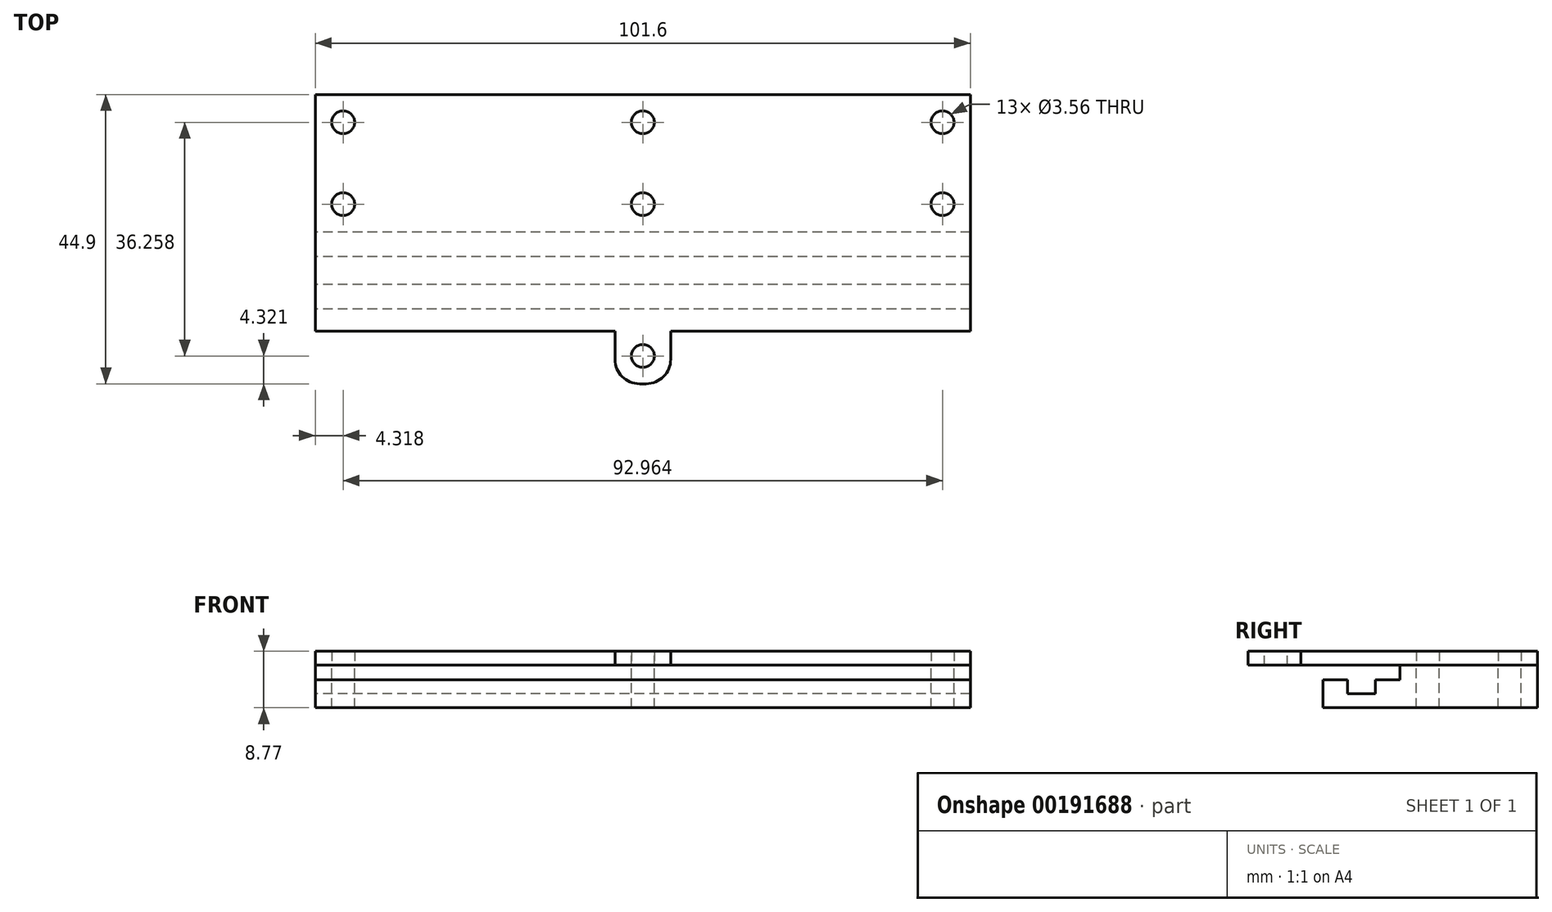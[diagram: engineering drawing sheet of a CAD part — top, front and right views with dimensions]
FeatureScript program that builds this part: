
annotation { "Feature Type Name" : "Feature", "Feature Type Description" : "" }
export const myFeature = defineFeature(function(context is Context, id is Id, definition is map)
    precondition{}
    {
        {
            var Q0;
            Q0=qCreatedBy(makeId("Right.planeOp"),FACE);
            var sketch = newSketch(context, id + "F0", { "sketchPlane" : qUnion([Q0])});
            skLineSegment(sketch, "E0.top", {"start": v(-6.45, -4.32) * mm, "end": v(26.83, -4.32) * mm});
            skLineSegment(sketch, "E0.left", {"start": v(-6.45, 0) * mm, "end": v(-6.45, -4.32) * mm});
            skLineSegment(sketch, "E0.right", {"start": v(26.83, 0) * mm, "end": v(26.83, -4.32) * mm});
            skLineSegment(sketch, "E1", {"start": v(-2.64, 0) * mm, "end": v(-2.64, -2.16) * mm});
            skLineSegment(sketch, "E2", {"start": v(-2.64, -2.16) * mm, "end": v(1.68, -2.16) * mm});
            skLineSegment(sketch, "E3", {"start": v(1.68, -2.16) * mm, "end": v(1.68, 0) * mm});
            skLineSegment(sketch, "E4", {"start": v(-6.45, 0) * mm, "end": v(-2.64, 0) * mm});
            skLineSegment(sketch, "E5", {"start": v(1.68, 0) * mm, "end": v(5.5, 0) * mm});
            skLineSegment(sketch, "E6", {"start": v(26.83, 0) * mm, "end": v(26.83, 2.29) * mm});
            skLineSegment(sketch, "E7", {"start": v(26.83, 2.29) * mm, "end": v(5.5, 2.29) * mm});
            skLineSegment(sketch, "E8", {"start": v(5.5, 2.29) * mm, "end": v(5.5, 0) * mm});
            skSolve(sketch);
        }
        {
            var Q0;
            Q0=makeQuery(id+"F0.imprint","IMPRINT",FACE,{"disambiguationData":[TD([[makeQuery(id+"F0.imprint","IMPRINT",EDGE,{"derivedFrom":sQuery(id+"F0.wireOp",EDGE,"E0.top")}),1.0]])]});
            extrude(context, id + "F1", {"entities" : qUnion([Q0]), "depth" : 101.6 * mm});
        }
        {
            var Q0;
            Q0=makeQuery(id+"F1.opExtrude","SWEPT_FACE",FACE,{"disambiguationData":[OSD([sQuery(id+"F0.wireOp",EDGE,"E7")])]});
            var sketch = newSketch(context, id + "F2", { "sketchPlane" : qUnion([Q0])});
            skCircle(sketch, "E9", {"center": v(97.28, 9.8) * mm, "radius": 1.78 * mm});
            skCircle(sketch, "E10", {"center": v(97.28, 22.5) * mm, "radius": 1.78 * mm});
            skCircle(sketch, "E11", {"center": v(4.32, 9.8) * mm, "radius": 1.78 * mm});
            skCircle(sketch, "E12", {"center": v(4.32, 22.5) * mm, "radius": 1.78 * mm});
            skCircle(sketch, "E13", {"center": v(50.8, 9.8) * mm, "radius": 1.78 * mm});
            skPoint(sketch, "E13.centerSnap0", {"position": v(50.8, 5.5) * mm});
            skCircle(sketch, "E14", {"center": v(50.8, 22.5) * mm, "radius": 1.78 * mm});
            skSolve(sketch);
        }
        {
            var Q0;
            Q0=qSketchRegion(id+"F2",true);
            extrude(context, id + "F3", {"entities" : qUnion([Q0]), "operationType" : NewBodyOperationType.REMOVE, "endBound" : BoundingType.THROUGH_ALL, "oppositeDirection" : true, "depth" : 25.4 * mm});
        }
        {
            var Q0;
            Q0=qCreatedBy(makeId("Right.planeOp"),FACE);
            var sketch = newSketch(context, id + "F4", { "sketchPlane" : qUnion([Q0])});
            skLineSegment(sketch, "E15", {"start": v(-9.88, 2.29) * mm, "end": v(-9.88, 4.45) * mm});
            skLineSegment(sketch, "E16.0", {"start": v(26.83, 2.29) * mm, "end": v(5.5, 2.29) * mm});
            skLineSegment(sketch, "E17", {"start": v(-9.88, 2.29) * mm, "end": v(26.83, 2.29) * mm});
            skLineSegment(sketch, "E18", {"start": v(26.83, 4.45) * mm, "end": v(26.83, 2.29) * mm});
            skLineSegment(sketch, "E19", {"start": v(26.83, 4.45) * mm, "end": v(-9.88, 4.45) * mm});
            skSolve(sketch);
        }
        {
            var Q0;
            {var subQ0=sQuery(id+"F4.wireOp",EDGE,"E15");Q0=makeQuery(id+"F4.imprint","IMPRINT",FACE,{"disambiguationData":[TD([[makeQuery(id+"F4.imprint","IMPRINT",EDGE,{"derivedFrom":subQ0}),-1.0]])]});}
            var Q1;
            Q1=makeQuery(id+"F1.opExtrude","CAP_FACE",FACE,{"disambiguationData":[OSD([sQuery(id+"F0.wireOp",EDGE,"E0.top"),sQuery(id+"F0.wireOp",EDGE,"E0.left"),sQuery(id+"F0.wireOp",EDGE,"E0.right"),sQuery(id+"F0.wireOp",EDGE,"E1"),sQuery(id+"F0.wireOp",EDGE,"E2"),sQuery(id+"F0.wireOp",EDGE,"E3"),sQuery(id+"F0.wireOp",EDGE,"E4"),sQuery(id+"F0.wireOp",EDGE,"E5"),sQuery(id+"F0.wireOp",EDGE,"E6"),sQuery(id+"F0.wireOp",EDGE,"E7"),sQuery(id+"F0.wireOp",EDGE,"E8")])],"isStart":false});
            extrude(context, id + "F5", {"entities" : qUnion([Q0]), "endBound" : BoundingType.UP_TO_SURFACE, "endBoundEntityFace" : qUnion([Q1]), "depth" : 25.4 * mm});
        }
        {
            var Q0;
            Q0=makeQuery(id+"F5.opExtrude","SWEPT_FACE",FACE,{"disambiguationData":[OSD([sQuery(id+"F4.wireOp",EDGE,"E17")])]});
            var sketch = newSketch(context, id + "F6", { "sketchPlane" : qUnion([Q0])});
            skCircle(sketch, "E20.0", {"center": v(97.28, -9.8) * mm, "radius": 1.78 * mm});
            skCircle(sketch, "E20.1", {"center": v(50.8, -9.8) * mm, "radius": 1.78 * mm});
            skCircle(sketch, "E20.2", {"center": v(4.32, -9.8) * mm, "radius": 1.78 * mm});
            skCircle(sketch, "E20.3", {"center": v(4.32, -22.5) * mm, "radius": 1.78 * mm});
            skCircle(sketch, "E20.4", {"center": v(50.8, -22.5) * mm, "radius": 1.78 * mm});
            skCircle(sketch, "E20.5", {"center": v(97.28, -22.5) * mm, "radius": 1.78 * mm});
            skSolve(sketch);
        }
        {
            var Q0;
            Q0=qSketchRegion(id+"F6",true);
            extrude(context, id + "F7", {"entities" : qUnion([Q0]), "operationType" : NewBodyOperationType.REMOVE, "endBound" : BoundingType.THROUGH_ALL, "oppositeDirection" : true, "depth" : 25.4 * mm});
        }
        {
            var Q0;
            Q0=makeQuery(id+"F5.opExtrude","SWEPT_FACE",FACE,{"disambiguationData":[OSD([sQuery(id+"F4.wireOp",EDGE,"E19")])]});
            var sketch = newSketch(context, id + "F8", { "sketchPlane" : qUnion([Q0])});
            skLineSegment(sketch, "E21.bottom", {"start": v(46.48, -9.88) * mm, "end": v(55.12, -9.88) * mm});
            skLineSegment(sketch, "E21.top", {"start": v(46.48, -18.07) * mm, "end": v(55.12, -18.07) * mm});
            skLineSegment(sketch, "E21.left", {"start": v(46.48, -9.88) * mm, "end": v(46.48, -18.07) * mm});
            skLineSegment(sketch, "E21.right", {"start": v(55.12, -9.88) * mm, "end": v(55.12, -18.07) * mm});
            skPoint(sketch, "E22", {"position": v(50.8, -18.07) * mm});
            skCircle(sketch, "E23", {"center": v(50.8, -13.75) * mm, "radius": 1.78 * mm});
            skSolve(sketch);
        }
        {
            var Q0;
            Q0=qSketchRegion(id+"F8",true);
            var Q1;
            Q1=makeQuery(id+"F5.opExtrude","SWEPT_FACE",FACE,{"disambiguationData":[OSD([sQuery(id+"F4.wireOp",EDGE,"E17")])]});
            extrude(context, id + "F9", {"entities" : qUnion([Q0]), "operationType" : NewBodyOperationType.ADD, "endBound" : BoundingType.UP_TO_SURFACE, "oppositeDirection" : true, "endBoundEntityFace" : qUnion([Q1]), "depth" : 25.4 * mm});
        }
        {
            var Q0;
            Q0=makeQuery(id+"F9.opExtrude","SWEPT_EDGE",EDGE,{"disambiguationData":[OSD([sQuery(id+"F8.wireOp",EDGE,"E21.top"),sQuery(id+"F8.wireOp",EDGE,"E21.right")])]});
            var Q1;
            Q1=makeQuery(id+"F9.opExtrude","SWEPT_EDGE",EDGE,{"disambiguationData":[OSD([sQuery(id+"F8.wireOp",EDGE,"E21.top"),sQuery(id+"F8.wireOp",EDGE,"E21.left")])]});
            fillet(context, id + "F10", {"entities" : qUnion([Q0, Q1]), "radius" : 3.8 * mm, "tangentPropagation" : true, "allowEdgeOverflow" : false});
        }
    });
